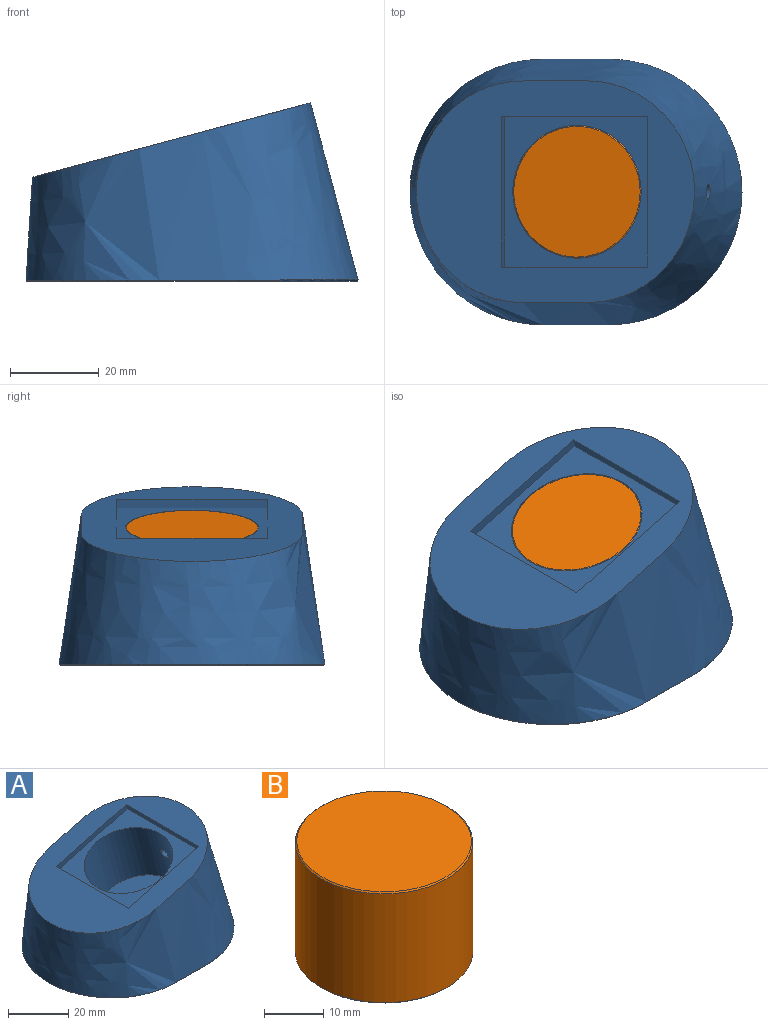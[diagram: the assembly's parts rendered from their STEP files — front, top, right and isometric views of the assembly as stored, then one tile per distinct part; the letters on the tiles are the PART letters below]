
ASSEMBLY  parts=2 mates=1
PART A: 15 faces, bbox 75x60x40.3 mm
  f0: bspline ~75x60mm, area 6503.6mm2, adj f2,f10,f11,f12,f13,f14
  f1: cylinder r=15mm len=34.93mm, axis (-0.26,0,0.97), area 2158.6mm2, adj f8,f9,f14
  f2: plane 62.79x50mm, normal (-0.26,0,0.97), area 1557.4mm2, adj f0,f4,f5,f6,f7
  f3: plane 74.53x59.54mm, normal (0,0,-1), area 3673.7mm2, adj f10,f11,f12,f13
  f4: plane 33.36x10.73mm, normal (0,1,0), area 68mm2, adj f2,f5,f7,f8
  f5: plane 34x1.93mm, normal (-0.97,0,-0.26), area 68mm2, adj f2,f4,f6,f8
  f6: plane 33.36x10.73mm, normal (0,-1,0), area 68mm2, adj f2,f5,f7,f8
  f7: plane 34x1.93mm, normal (0.97,0,0.26), area 68mm2, adj f2,f4,f6,f8
  f8: plane 34x32.84mm, normal (-0.26,0,0.97), area 449.1mm2, adj f1,f4,f5,f6,f7
  f9: plane 30x28.98mm, normal (-0.26,0,0.97), area 706.9mm2, adj f1
  f10: bspline ~15x0.25mm, area 4.8mm2, adj f0,f3,f11,f12
  f11: bspline ~59.93x29.93mm, area 30.9mm2, adj f0,f3,f10,f13
  f12: bspline ~59.92x29.99mm, area 29.4mm2, adj f0,f3,f10,f13
  f13: bspline ~15x0.25mm, area 4.8mm2, adj f0,f3,f11,f12
  f14: cylinder r=1.7mm len=13.44mm, axis (0.97,0,0.26), area 138.9mm2, adj f0,f1
PART B: 5 faces, bbox 30x30x23 mm
  f0: cylinder r=15mm len=30mm, axis (0,0,1), area 2120.6mm2, adj f3,f4
  f1: plane 29.5x29.5mm, normal (0,0,-1), area 683.5mm2, adj f4
  f2: plane 29.5x29.5mm, normal (0,0,1), area 683.5mm2, adj f3
  f3: cone r=14.75mm half-angle=45deg, axis (0,0,-1), area 33mm2, adj f0,f2
  f4: cone r=15mm half-angle=45deg, axis (0,0,1), area 33mm2, adj f0,f1
PLACE A t=(-4.69,0,0.45)mm
PLACE B rot(axis=(0,-1,0),15deg) t=(-4.5,0,31.5)mm
MATE fastened B.f0 <-> A.f1  axis (0.26,0,-0.97) through (1.45,0,9.28)mm
